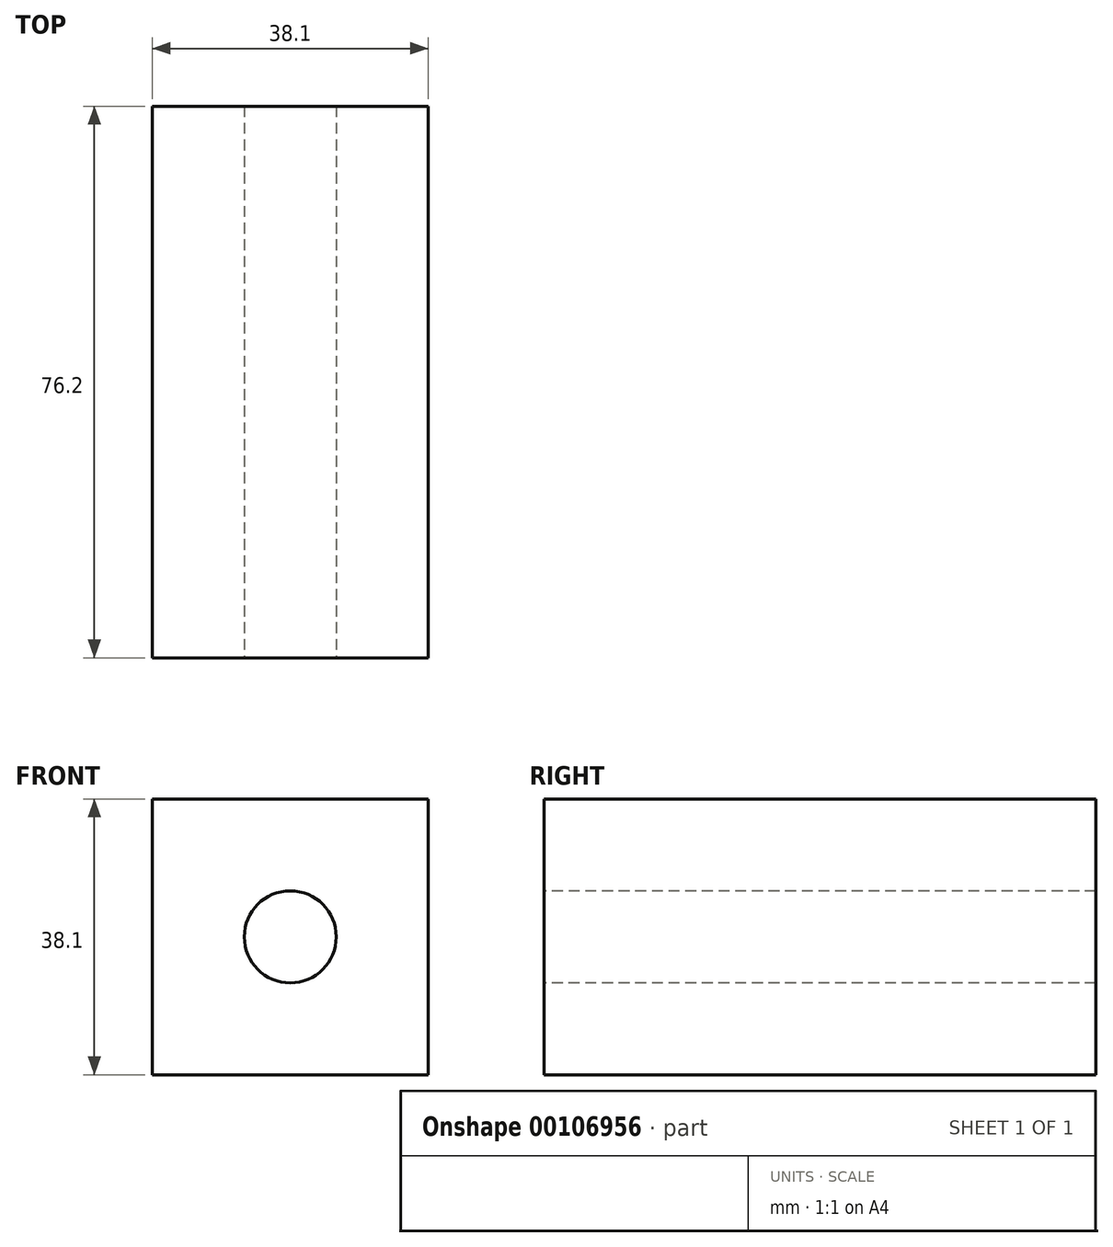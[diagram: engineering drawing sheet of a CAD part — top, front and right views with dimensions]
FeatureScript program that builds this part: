
annotation { "Feature Type Name" : "Feature", "Feature Type Description" : "" }
export const myFeature = defineFeature(function(context is Context, id is Id, definition is map)
    precondition{}
    {
        {
            var Q0;
            Q0=qCreatedBy(makeId("Front.planeOp"),FACE);
            var sketch = newSketch(context, id + "F0", { "sketchPlane" : qUnion([Q0])});
            skLineSegment(sketch, "E0.bottom", {"start": v(38.1, -38.1) * mm, "end": v(-38.1, -38.1) * mm});
            skLineSegment(sketch, "E0.top", {"start": v(38.1, 38.1) * mm, "end": v(-38.1, 38.1) * mm});
            skLineSegment(sketch, "E0.left", {"start": v(38.1, -38.1) * mm, "end": v(38.1, 38.1) * mm});
            skLineSegment(sketch, "E0.right", {"start": v(-38.1, -38.1) * mm, "end": v(-38.1, 38.1) * mm});
            skPoint(sketch, "E0.middle", {"position": v(0, 0) * mm});
            skLineSegment(sketch, "E1.bottom", {"start": v(19.05, -19.05) * mm, "end": v(-19.05, -19.05) * mm});
            skLineSegment(sketch, "E1.top", {"start": v(19.05, 19.05) * mm, "end": v(-19.05, 19.05) * mm});
            skLineSegment(sketch, "E1.left", {"start": v(19.05, -19.05) * mm, "end": v(19.05, 19.05) * mm});
            skLineSegment(sketch, "E1.right", {"start": v(-19.05, -19.05) * mm, "end": v(-19.05, 19.05) * mm});
            skSolve(sketch);
        }
        {
            var Q0;
            Q0=makeQuery(id+"F0.imprint","IMPRINT",FACE,{"disambiguationData":[TD([[makeQuery(id+"F0.imprint","IMPRINT",EDGE,{"derivedFrom":sQuery(id+"F0.wireOp",EDGE,"E1.bottom")}),-1.0]])]});
            extrude(context, id + "F1", {"entities" : qUnion([Q0]), "depth" : 76.2 * mm});
        }
        {
            var Q0;
            Q0=makeQuery(id+"F1.opExtrude","CAP_FACE",FACE,{"disambiguationData":[OSD([sQuery(id+"F0.wireOp",EDGE,"E1.bottom"),sQuery(id+"F0.wireOp",EDGE,"E1.top"),sQuery(id+"F0.wireOp",EDGE,"E1.left"),sQuery(id+"F0.wireOp",EDGE,"E1.right")])],"isStart":false});
            var sketch = newSketch(context, id + "F2", { "sketchPlane" : qUnion([Q0])});
            skCircle(sketch, "E2", {"center": v(0, 0) * mm, "radius": 12.7 * mm});
            skSolve(sketch);
        }
        {
            var Q0;
            Q0=sQuery(id+"F2.wireOp",VERTEX,"E2.center");
            var Q1;
            Q1=makeQuery(id+"F1.opExtrude","SWEPT_BODY",BODY,{"disambiguationData":[OSD([sQuery(id+"F0.wireOp",EDGE,"E1.bottom"),sQuery(id+"F0.wireOp",EDGE,"E1.top"),sQuery(id+"F0.wireOp",EDGE,"E1.left"),sQuery(id+"F0.wireOp",EDGE,"E1.right")])]});
            hole(context, id + "F3", {"style" : HoleStyle.SIMPLE, "endStyle" : HoleEndStyle.THROUGH, "holeDiameter" : 12.7 * mm, "locations" : qUnion([Q0]), "scope" : qUnion([Q1]), "isTappedThrough" : true});
        }
    });
